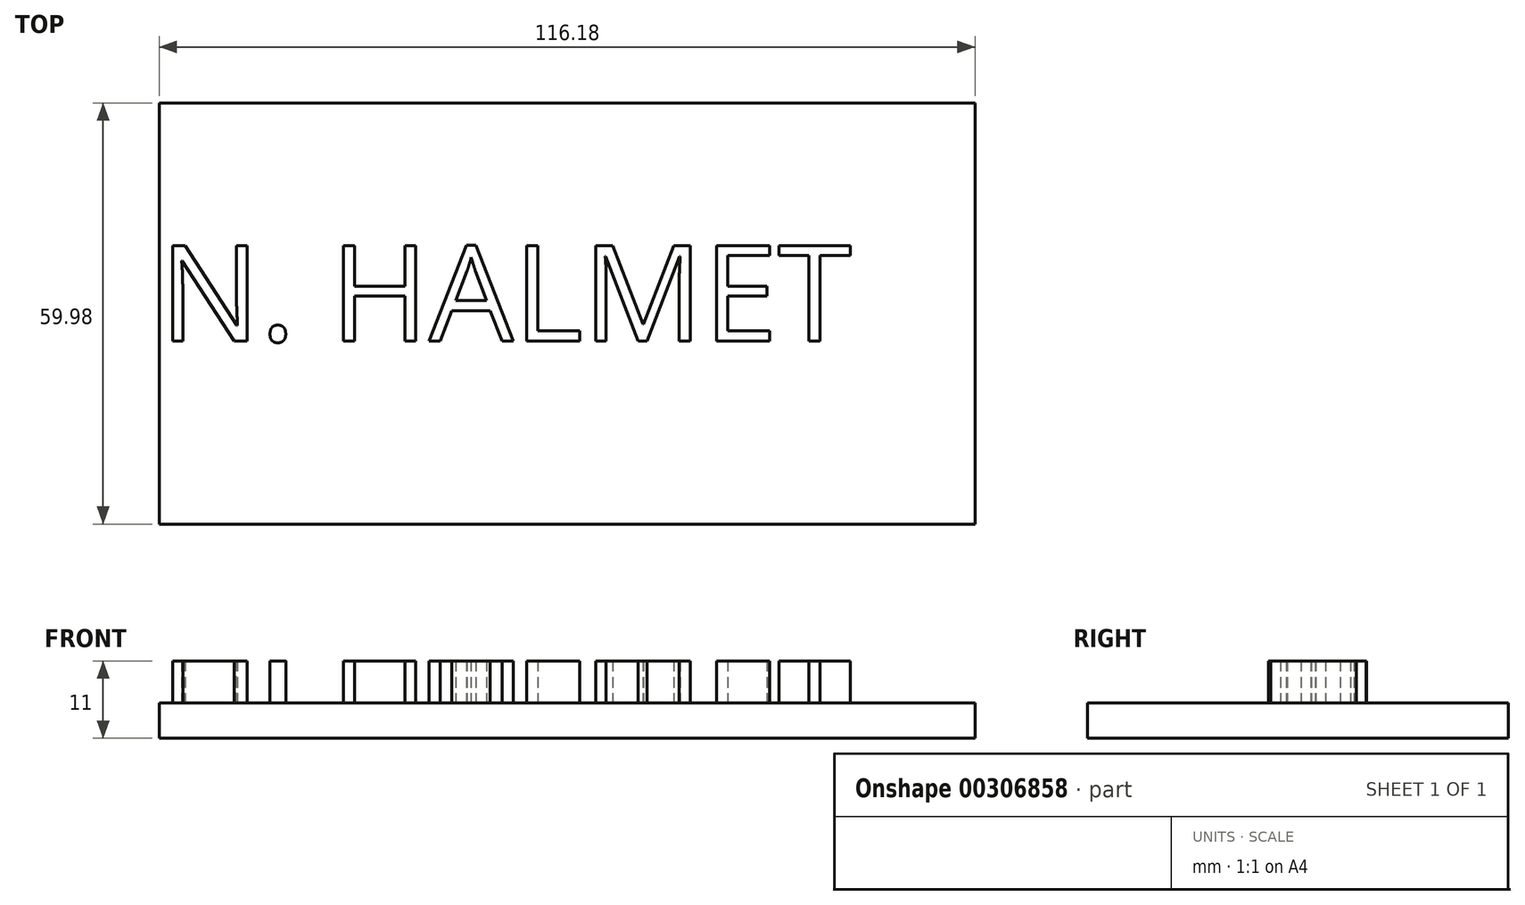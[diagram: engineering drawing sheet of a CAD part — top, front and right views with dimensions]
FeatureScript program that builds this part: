
annotation { "Feature Type Name" : "Feature", "Feature Type Description" : "" }
export const myFeature = defineFeature(function(context is Context, id is Id, definition is map)
    precondition{}
    {
        {
            var Q0;
            Q0=qCreatedBy(makeId("Top.planeOp"),FACE);
            var sketch = newSketch(context, id + "F0", { "sketchPlane" : qUnion([Q0])});
            skLineSegment(sketch, "E0.bottom", {"start": v(-116.18, -8.9) * mm, "end": v(0, -8.9) * mm});
            skLineSegment(sketch, "E0.top", {"start": v(-116.18, 51.08) * mm, "end": v(0, 51.08) * mm});
            skLineSegment(sketch, "E0.left", {"start": v(-116.18, -8.9) * mm, "end": v(-116.18, 51.08) * mm});
            skLineSegment(sketch, "E0.right", {"start": v(0, -8.9) * mm, "end": v(0, 51.08) * mm});
            skSolve(sketch);
        }
        {
            var Q0;
            Q0=makeQuery(id+"F0.imprint","IMPRINT",FACE,{"disambiguationData":[TD([[makeQuery(id+"F0.imprint","IMPRINT",EDGE,{"derivedFrom":sQuery(id+"F0.wireOp",EDGE,"E0.bottom")}),1.0]])]});
            extrude(context, id + "F1", {"entities" : qUnion([Q0]), "depth" : 5 * mm});
        }
        {
            var Q0;
            Q0=makeQuery(id+"F1.opExtrude","CAP_FACE",FACE,{"disambiguationData":[OSD([sQuery(id+"F0.wireOp",EDGE,"E0.bottom"),sQuery(id+"F0.wireOp",EDGE,"E0.top"),sQuery(id+"F0.wireOp",EDGE,"E0.left"),sQuery(id+"F0.wireOp",EDGE,"E0.right")])],"isStart":false});
            var sketch = newSketch(context, id + "F2", { "sketchPlane" : qUnion([Q0])});
            skText(sketch, "E1", { "text": "N. HALMET", "fontName": "OpenSans-Regular.ttf"});
            const initialGuessF2  = {"E1": [-0.11618, 0.0172, 1, 0, 0.0137]};
            skSetInitialGuess(sketch, initialGuessF2);
            skSolve(sketch);
        }
        {
            var Q0;
            Q0 = qSketchRegion(id + "F2", true);
            extrude(context, id + "F3", {"entities" : qUnion([Q0]), "operationType" : NewBodyOperationType.ADD, "depth" : 6 * mm});
        }
    });
